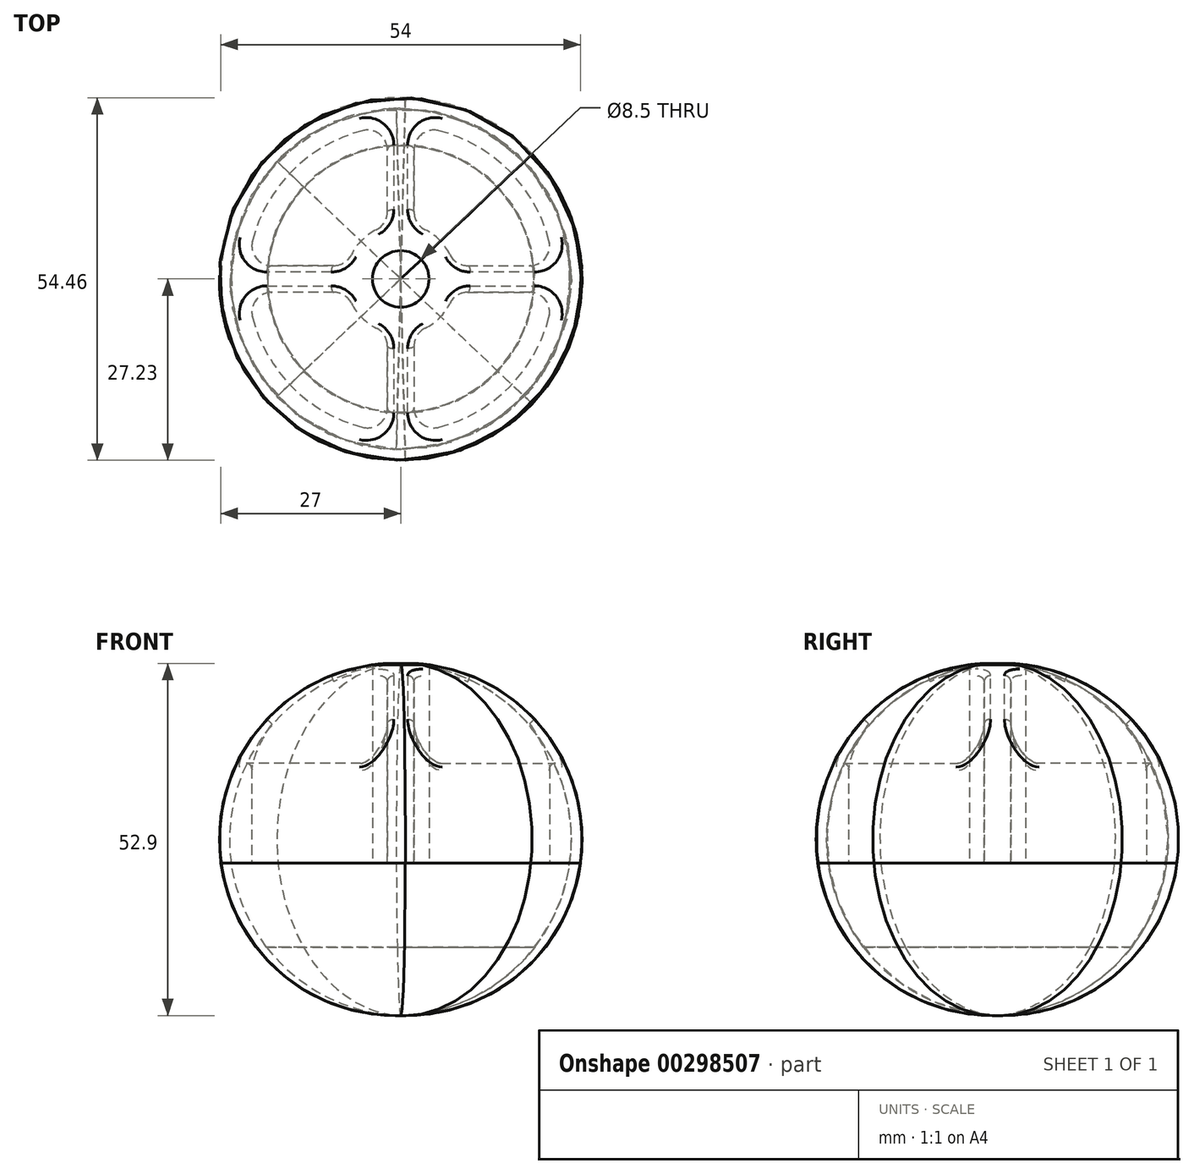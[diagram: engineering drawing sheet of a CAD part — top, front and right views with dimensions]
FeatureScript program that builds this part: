
annotation { "Feature Type Name" : "Feature", "Feature Type Description" : "" }
export const myFeature = defineFeature(function(context is Context, id is Id, definition is map)
    precondition{}
    {
        {
            var Q0;
            Q0=qCreatedBy(makeId("Top.planeOp"),FACE);
            var sketch = newSketch(context, id + "F0", { "sketchPlane" : qUnion([Q0])});
            skCircle(sketch, "E0", {"center": v(0, 0) * mm, "radius": 27 * mm});
            skSolve(sketch);
        }
        {
            var Q0;
            Q0=qCreatedBy(makeId("Right.planeOp"),FACE);
            var sketch = newSketch(context, id + "F1", { "sketchPlane" : qUnion([Q0])});
            skLineSegment(sketch, "E1", {"start": v(0, 0) * mm, "end": v(0, 30) * mm});
            skLineSegment(sketch, "E2", {"start": v(27, 0) * mm, "end": v(0, 0) * mm});
            skArc(sketch, "E3", {"start": v(27, 0) * mm, "mid": v(20.45, 21.26) * mm, "end": v(0, 30) * mm});
            skSolve(sketch);
        }
        {
            var Q0;
            Q0=makeQuery(id+"F1.imprint","IMPRINT",FACE,{"disambiguationData":[TD([[makeQuery(id+"F1.imprint","IMPRINT",EDGE,{"derivedFrom":sQuery(id+"F1.wireOp",EDGE,"E1")}),-1.0]])]});
            var Q1;
            Q1=sQuery(id+"F0.wireOp",EDGE,"E0");
            sweep(context, id + "F2", {"profiles" : qUnion([Q0]), "path" : qUnion([Q1])});
        }
        {
            var Q0;
            Q0=makeQuery(id+"F2.opSweep","SWEPT_FACE",FACE,{"disambiguationData":[OSD([sQuery(id+"F0.wireOp",EDGE,"E0"),sQuery(id+"F1.wireOp",EDGE,"E2")])]});
            var sketch = newSketch(context, id + "F3", { "sketchPlane" : qUnion([Q0])});
            skCircle(sketch, "E4", {"center": v(0, 0) * mm, "radius": 4.25 * mm});
            skCircle(sketch, "E5.0", {"center": v(0, 0) * mm, "radius": 23 * mm});
            skCircle(sketch, "E6.0", {"center": v(0, 0) * mm, "radius": 8.25 * mm});
            skLineSegment(sketch, "E7", {"start": v(0, 0) * mm, "end": v(-30.25, 0) * mm, "construction": true});
            skLineSegment(sketch, "E8", {"start": v(-8, -2) * mm, "end": v(-22.91, -2) * mm});
            skLineSegment(sketch, "E9", {"start": v(-8, 2) * mm, "end": v(-22.91, 2) * mm});
            skLineSegment(sketch, "E10.1.0", {"start": v(2, -8) * mm, "end": v(2, -22.91) * mm});
            skLineSegment(sketch, "E10.1.1", {"start": v(-2, -8) * mm, "end": v(-2, -22.91) * mm});
            skLineSegment(sketch, "E10.2.0", {"start": v(8, 2) * mm, "end": v(22.91, 2) * mm});
            skLineSegment(sketch, "E10.2.1", {"start": v(8, -2) * mm, "end": v(22.91, -2) * mm});
            skLineSegment(sketch, "E10.3.0", {"start": v(-2, 8) * mm, "end": v(-2, 22.91) * mm});
            skLineSegment(sketch, "E10.3.1", {"start": v(2, 8) * mm, "end": v(2, 22.91) * mm});
            skSolve(sketch);
        }
        {
            var Q0;
            {var subQ0=sQuery(id+"F3.wireOp",EDGE,"E8");Q0=makeQuery(id+"F3.imprint","IMPRINT",FACE,{"disambiguationData":[TD([[makeQuery(id+"F3.imprint","IMPRINT",EDGE,{"derivedFrom":subQ0}),1.0]])]});}
            var Q1;
            {var subQ0=sQuery(id+"F3.wireOp",EDGE,"E9");Q1=makeQuery(id+"F3.imprint","IMPRINT",FACE,{"disambiguationData":[TD([[makeQuery(id+"F3.imprint","IMPRINT",EDGE,{"derivedFrom":subQ0}),-1.0]])]});}
            var Q2;
            {var subQ0=sQuery(id+"F3.wireOp",EDGE,"E10.2.0");Q2=makeQuery(id+"F3.imprint","IMPRINT",FACE,{"disambiguationData":[TD([[makeQuery(id+"F3.imprint","IMPRINT",EDGE,{"derivedFrom":subQ0}),1.0]])]});}
            var Q3;
            {var subQ0=sQuery(id+"F3.wireOp",EDGE,"E10.1.0");Q3=makeQuery(id+"F3.imprint","IMPRINT",FACE,{"disambiguationData":[TD([[makeQuery(id+"F3.imprint","IMPRINT",EDGE,{"derivedFrom":subQ0}),1.0]])]});}
            var Q4;
            Q4=makeQuery(id+"F3.imprint","IMPRINT",FACE,{"disambiguationData":[TD([[makeQuery(id+"F3.imprint","IMPRINT",EDGE,{"derivedFrom":sQuery(id+"F3.wireOp",EDGE,"E4")}),1.0]])]});
            extrude(context, id + "F4", {"entities" : qUnion([Q0, Q1, Q2, Q3, Q4]), "operationType" : NewBodyOperationType.REMOVE, "endBound" : BoundingType.THROUGH_ALL, "oppositeDirection" : true, "depth" : 25 * mm});
        }
        {
            var Q0;
            Q0=makeQuery(id+"F4.boolean.opBoolean","COPY",EDGE,{"derivedFrom":makeQuery(id+"F4.opExtrude","SWEPT_EDGE",EDGE,{"disambiguationData":[OSD([sQuery(id+"F3.wireOp",EDGE,"E6.0"),sQuery(id+"F3.wireOp",EDGE,"E10.1.1")])]})});
            var Q1;
            Q1=makeQuery(id+"F4.boolean.opBoolean","COPY",EDGE,{"derivedFrom":makeQuery(id+"F4.opExtrude","SWEPT_EDGE",EDGE,{"disambiguationData":[OSD([sQuery(id+"F3.wireOp",EDGE,"E6.0"),sQuery(id+"F3.wireOp",EDGE,"E8")])]})});
            var Q2;
            Q2=makeQuery(id+"F4.boolean.opBoolean","COPY",EDGE,{"derivedFrom":makeQuery(id+"F4.opExtrude","SWEPT_EDGE",EDGE,{"disambiguationData":[OSD([sQuery(id+"F3.wireOp",EDGE,"E6.0"),sQuery(id+"F3.wireOp",EDGE,"E10.3.0")])]})});
            var Q3;
            Q3=makeQuery(id+"F4.boolean.opBoolean","COPY",EDGE,{"derivedFrom":makeQuery(id+"F4.opExtrude","SWEPT_EDGE",EDGE,{"disambiguationData":[OSD([sQuery(id+"F3.wireOp",EDGE,"E6.0"),sQuery(id+"F3.wireOp",EDGE,"E9")])]})});
            var Q4;
            Q4=makeQuery(id+"F4.boolean.opBoolean","COPY",EDGE,{"derivedFrom":makeQuery(id+"F4.opExtrude","SWEPT_EDGE",EDGE,{"disambiguationData":[OSD([sQuery(id+"F3.wireOp",EDGE,"E6.0"),sQuery(id+"F3.wireOp",EDGE,"E10.3.1")])]})});
            var Q5;
            Q5=makeQuery(id+"F4.boolean.opBoolean","COPY",EDGE,{"derivedFrom":makeQuery(id+"F4.opExtrude","SWEPT_EDGE",EDGE,{"disambiguationData":[OSD([sQuery(id+"F3.wireOp",EDGE,"E6.0"),sQuery(id+"F3.wireOp",EDGE,"E10.2.0")])]})});
            var Q6;
            Q6=makeQuery(id+"F4.boolean.opBoolean","COPY",EDGE,{"derivedFrom":makeQuery(id+"F4.opExtrude","SWEPT_EDGE",EDGE,{"disambiguationData":[OSD([sQuery(id+"F3.wireOp",EDGE,"E6.0"),sQuery(id+"F3.wireOp",EDGE,"E10.2.1")])]})});
            var Q7;
            Q7=makeQuery(id+"F4.boolean.opBoolean","COPY",EDGE,{"derivedFrom":makeQuery(id+"F4.opExtrude","SWEPT_EDGE",EDGE,{"disambiguationData":[OSD([sQuery(id+"F3.wireOp",EDGE,"E6.0"),sQuery(id+"F3.wireOp",EDGE,"E10.1.0")])]})});
            var Q8;
            Q8=makeQuery(id+"F4.boolean.opBoolean","COPY",EDGE,{"derivedFrom":makeQuery(id+"F4.opExtrude","SWEPT_EDGE",EDGE,{"disambiguationData":[OSD([sQuery(id+"F3.wireOp",EDGE,"E5.0"),sQuery(id+"F3.wireOp",EDGE,"E10.1.1")])]})});
            var Q9;
            Q9=makeQuery(id+"F4.boolean.opBoolean","COPY",EDGE,{"derivedFrom":makeQuery(id+"F4.opExtrude","SWEPT_EDGE",EDGE,{"disambiguationData":[OSD([sQuery(id+"F3.wireOp",EDGE,"E5.0"),sQuery(id+"F3.wireOp",EDGE,"E8")])]})});
            var Q10;
            Q10=makeQuery(id+"F4.boolean.opBoolean","COPY",EDGE,{"derivedFrom":makeQuery(id+"F4.opExtrude","SWEPT_EDGE",EDGE,{"disambiguationData":[OSD([sQuery(id+"F3.wireOp",EDGE,"E5.0"),sQuery(id+"F3.wireOp",EDGE,"E9")])]})});
            var Q11;
            Q11=makeQuery(id+"F4.boolean.opBoolean","COPY",EDGE,{"derivedFrom":makeQuery(id+"F4.opExtrude","SWEPT_EDGE",EDGE,{"disambiguationData":[OSD([sQuery(id+"F3.wireOp",EDGE,"E5.0"),sQuery(id+"F3.wireOp",EDGE,"E10.3.0")])]})});
            var Q12;
            Q12=makeQuery(id+"F4.boolean.opBoolean","COPY",EDGE,{"derivedFrom":makeQuery(id+"F4.opExtrude","SWEPT_EDGE",EDGE,{"disambiguationData":[OSD([sQuery(id+"F3.wireOp",EDGE,"E5.0"),sQuery(id+"F3.wireOp",EDGE,"E10.3.1")])]})});
            var Q13;
            Q13=makeQuery(id+"F4.boolean.opBoolean","COPY",EDGE,{"derivedFrom":makeQuery(id+"F4.opExtrude","SWEPT_EDGE",EDGE,{"disambiguationData":[OSD([sQuery(id+"F3.wireOp",EDGE,"E5.0"),sQuery(id+"F3.wireOp",EDGE,"E10.2.0")])]})});
            var Q14;
            Q14=makeQuery(id+"F4.boolean.opBoolean","COPY",EDGE,{"derivedFrom":makeQuery(id+"F4.opExtrude","SWEPT_EDGE",EDGE,{"disambiguationData":[OSD([sQuery(id+"F3.wireOp",EDGE,"E5.0"),sQuery(id+"F3.wireOp",EDGE,"E10.2.1")])]})});
            var Q15;
            Q15=makeQuery(id+"F4.boolean.opBoolean","COPY",EDGE,{"derivedFrom":makeQuery(id+"F4.opExtrude","SWEPT_EDGE",EDGE,{"disambiguationData":[OSD([sQuery(id+"F3.wireOp",EDGE,"E5.0"),sQuery(id+"F3.wireOp",EDGE,"E10.1.0")])]})});
            fillet(context, id + "F5", {"entities" : qUnion([Q0, Q1, Q2, Q3, Q4, Q5, Q6, Q7, Q8, Q9, Q10, Q11, Q12, Q13, Q14, Q15]), "radius" : 3 * mm, "tangentPropagation" : true, "allowEdgeOverflow" : false});
        }
        {
            var Q0;
            Q0=makeQuery(id+"F5.opFillet","BLEND_EDGE",EDGE,{"blendedFrom":[makeQuery(id+"F4.boolean.opBoolean","COPY",EDGE,{"derivedFrom":makeQuery(id+"F4.opExtrude","SWEPT_EDGE",EDGE,{"disambiguationData":[OSD([sQuery(id+"F3.wireOp",EDGE,"E6.0"),sQuery(id+"F3.wireOp",EDGE,"E10.1.1")])]})}),makeQuery(id+"F2.opSweep","SWEPT_FACE",FACE,{"disambiguationData":[OSD([sQuery(id+"F0.wireOp",EDGE,"E0"),sQuery(id+"F1.wireOp",EDGE,"E3")])]})],"blendedInto":[makeQuery(id+"F2.opSweep","SWEPT_FACE",FACE,{"disambiguationData":[OSD([sQuery(id+"F0.wireOp",EDGE,"E0"),sQuery(id+"F1.wireOp",EDGE,"E3")])]})]});
            var Q1;
            Q1=makeQuery(id+"F5.opFillet","BLEND_EDGE",EDGE,{"blendedFrom":[makeQuery(id+"F4.boolean.opBoolean","COPY",EDGE,{"derivedFrom":makeQuery(id+"F4.opExtrude","SWEPT_EDGE",EDGE,{"disambiguationData":[OSD([sQuery(id+"F3.wireOp",EDGE,"E6.0"),sQuery(id+"F3.wireOp",EDGE,"E10.3.1")])]})}),makeQuery(id+"F2.opSweep","SWEPT_FACE",FACE,{"disambiguationData":[OSD([sQuery(id+"F0.wireOp",EDGE,"E0"),sQuery(id+"F1.wireOp",EDGE,"E3")])]})],"blendedInto":[makeQuery(id+"F2.opSweep","SWEPT_FACE",FACE,{"disambiguationData":[OSD([sQuery(id+"F0.wireOp",EDGE,"E0"),sQuery(id+"F1.wireOp",EDGE,"E3")])]})]});
            var Q2;
            Q2=makeQuery(id+"F5.opFillet","BLEND_EDGE",EDGE,{"blendedFrom":[makeQuery(id+"F4.boolean.opBoolean","COPY",EDGE,{"derivedFrom":makeQuery(id+"F4.opExtrude","SWEPT_EDGE",EDGE,{"disambiguationData":[OSD([sQuery(id+"F3.wireOp",EDGE,"E6.0"),sQuery(id+"F3.wireOp",EDGE,"E10.3.0")])]})}),makeQuery(id+"F2.opSweep","SWEPT_FACE",FACE,{"disambiguationData":[OSD([sQuery(id+"F0.wireOp",EDGE,"E0"),sQuery(id+"F1.wireOp",EDGE,"E3")])]})],"blendedInto":[makeQuery(id+"F2.opSweep","SWEPT_FACE",FACE,{"disambiguationData":[OSD([sQuery(id+"F0.wireOp",EDGE,"E0"),sQuery(id+"F1.wireOp",EDGE,"E3")])]})]});
            var Q3;
            Q3=makeQuery(id+"F5.opFillet","BLEND_EDGE",EDGE,{"blendedFrom":[makeQuery(id+"F4.boolean.opBoolean","COPY",EDGE,{"derivedFrom":makeQuery(id+"F4.opExtrude","SWEPT_EDGE",EDGE,{"disambiguationData":[OSD([sQuery(id+"F3.wireOp",EDGE,"E6.0"),sQuery(id+"F3.wireOp",EDGE,"E10.2.1")])]})}),makeQuery(id+"F2.opSweep","SWEPT_FACE",FACE,{"disambiguationData":[OSD([sQuery(id+"F0.wireOp",EDGE,"E0"),sQuery(id+"F1.wireOp",EDGE,"E3")])]})],"blendedInto":[makeQuery(id+"F2.opSweep","SWEPT_FACE",FACE,{"disambiguationData":[OSD([sQuery(id+"F0.wireOp",EDGE,"E0"),sQuery(id+"F1.wireOp",EDGE,"E3")])]})]});
            var Q4;
            Q4=makeQuery(id+"F4.boolean.opBoolean","COPY",EDGE,{"derivedFrom":makeQuery(id+"F4.opExtrude","CAP_EDGE",EDGE,{"disambiguationData":[OSD([sQuery(id+"F3.wireOp",EDGE,"E4")])],"isStart":true})});
            fillet(context, id + "F6", {"entities" : qUnion([Q0, Q1, Q2, Q3, Q4]), "radius" : 1 * mm, "tangentPropagation" : true, "allowEdgeOverflow" : false});
        }
    });
